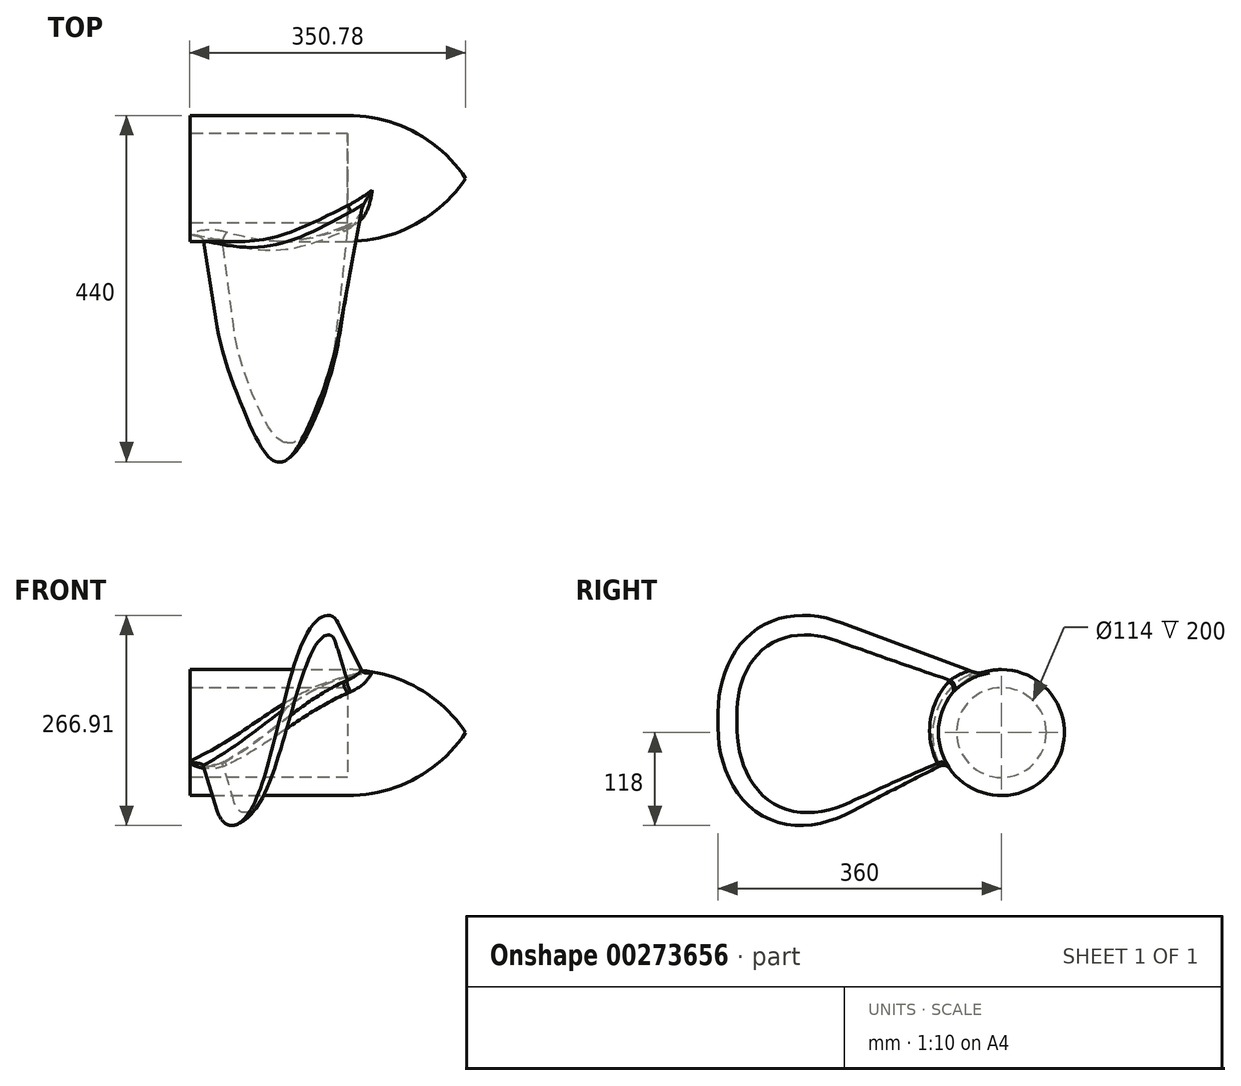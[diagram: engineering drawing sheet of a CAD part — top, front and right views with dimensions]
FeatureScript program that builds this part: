
annotation { "Feature Type Name" : "Feature", "Feature Type Description" : "" }
export const myFeature = defineFeature(function(context is Context, id is Id, definition is map)
    precondition{}
    {
        {
            var Q0;
            Q0=qCreatedBy(makeId("Front.planeOp"),FACE);
            var sketch = newSketch(context, id + "F0", { "sketchPlane" : qUnion([Q0])});
            skLineSegment(sketch, "E0", {"start": v(350, 0) * mm, "end": v(0, 0) * mm});
            skLineSegment(sketch, "E1", {"start": v(0, 0) * mm, "end": v(0, 80) * mm});
            skLineSegment(sketch, "E2", {"start": v(0, 80) * mm, "end": v(200, 80) * mm});
            skArc(sketch, "E3", {"start": v(200, 80) * mm, "mid": v(285, 58.75) * mm, "end": v(350, 0) * mm});
            skSolve(sketch);
        }
        {
            var Q0;
            Q0=makeQuery(id+"F0.imprint","IMPRINT",FACE,{"disambiguationData":[TD([[makeQuery(id+"F0.imprint","IMPRINT",EDGE,{"derivedFrom":sQuery(id+"F0.wireOp",EDGE,"E0")}),-1.0]])]});
            var Q1;
            Q1=sQuery(id+"F0.wireOp",EDGE,"E0");
            revolve(context, id + "F1", {"entities" : qUnion([Q0]), "axis" : qUnion([Q1]), "revolveType" : RevolveType.FULL});
        }
        {
            var Q0;
            Q0=qCreatedBy(makeId("Front.planeOp"),FACE);
            var sketch = newSketch(context, id + "F2", { "sketchPlane" : qUnion([Q0])});
            skLineSegment(sketch, "E4", {"start": v(3.9, 0) * mm, "end": v(225, 63.4) * mm});
            skLineSegment(sketch, "E5", {"start": v(225, 63.4) * mm, "end": v(228.3, 51.86) * mm});
            skLineSegment(sketch, "E6", {"start": v(228.3, 51.86) * mm, "end": v(7.22, -11.54) * mm});
            skLineSegment(sketch, "E7", {"start": v(7.22, -11.54) * mm, "end": v(3.9, 0) * mm});
            skSolve(sketch);
        }
        {
            var Q0;
            Q0=qCreatedBy(makeId("Front.planeOp"),FACE);
            cPlane(context, id + "F3", {"entities" : qUnion([Q0]), "cplaneType" : CPlaneType.OFFSET, "offset" : 360 * mm, "width" : 150 * mm, "height" : 150 * mm});
        }
        {
            var Q0;
            Q0=qCreatedBy(id+"F3.planeOp",FACE);
            var sketch = newSketch(context, id + "F4", { "sketchPlane" : qUnion([Q0])});
            skLineSegment(sketch, "E8", {"start": v(170.41, 195.22) * mm, "end": v(73.64, -192.9) * mm});
            skLineSegment(sketch, "E9", {"start": v(73.64, -192.9) * mm, "end": v(62, -190) * mm});
            skLineSegment(sketch, "E10", {"start": v(62, -190) * mm, "end": v(158.77, 198.12) * mm});
            skLineSegment(sketch, "E11", {"start": v(158.77, 198.12) * mm, "end": v(170.41, 195.22) * mm});
            skSolve(sketch);
        }
        {
            var Q1;
            Q1=makeQuery(id+"F4.imprint","IMPRINT",FACE,{"disambiguationData":[TD([[makeQuery(id+"F4.imprint","IMPRINT",EDGE,{"derivedFrom":sQuery(id+"F4.wireOp",EDGE,"E8")}),-1.0]])]});
            var Q2;
            Q2 = qSketchRegion(id + "F2", true);
            loft(context, id + "F5", {"operationType" : NewBodyOperationType.ADD, "sheetProfilesArray" : [{ "sheetProfileEntities" : qUnion([Q1]) }, { "sheetProfileEntities" : qUnion([Q2]) }]});
        }
        {
            var Q0;
            Q0=makeQuery(id+"F5.opLoft","MID_CAP_EDGE",EDGE,{"disambiguationData":[OSD([sQuery(id+"F4.wireOp",EDGE,"E8"),sQuery(id+"F4.wireOp",EDGE,"E10"),sQuery(id+"F4.wireOp",EDGE,"E11")])],"capPos":0.0});
            var Q1;
            Q1=makeQuery(id+"F5.opLoft","MID_CAP_EDGE",EDGE,{"disambiguationData":[OSD([sQuery(id+"F4.wireOp",EDGE,"E8"),sQuery(id+"F4.wireOp",EDGE,"E9"),sQuery(id+"F4.wireOp",EDGE,"E10")])],"capPos":0.0});
            fillet(context, id + "F6", {"entities" : qUnion([Q0, Q1]), "radius" : 135 * mm, "tangentPropagation" : true, "allowEdgeOverflow" : false});
        }
        {
            var Q0;
            Q0=makeQuery(id+"F1.opRevolve","SWEPT_FACE",FACE,{"disambiguationData":[OSD([sQuery(id+"F0.wireOp",EDGE,"E1")])]});
            var sketch = newSketch(context, id + "F7", { "sketchPlane" : qUnion([Q0])});
            skCircle(sketch, "E12", {"center": v(0, 0) * mm, "radius": 57 * mm});
            skSolve(sketch);
        }
        {
            var Q0;
            Q0=makeQuery(id+"F7.imprint","IMPRINT",FACE,{"disambiguationData":[TD([[makeQuery(id+"F7.imprint","IMPRINT",EDGE,{"derivedFrom":sQuery(id+"F7.wireOp",EDGE,"E12")}),1.0]])]});
            extrude(context, id + "F8", {"entities" : qUnion([Q0]), "operationType" : NewBodyOperationType.REMOVE, "oppositeDirection" : true, "depth" : 200 * mm});
        }
        {
            var Q0;
            {var subQ0=sQuery(id+"F4.wireOp",EDGE,"E9");var subQ1=sQuery(id+"F4.wireOp",EDGE,"E8");Q0=makeQuery(id+"F6.opFillet","BLEND_EDGE",EDGE,{"blendedFrom":[makeQuery(id+"F5.opLoft","MID_CAP_EDGE",EDGE,{"disambiguationData":[OSD([subQ1,subQ0,sQuery(id+"F4.wireOp",EDGE,"E10")])],"capPos":0.0}),makeQuery(id+"F5.opLoft","SWEPT_FACE",FACE,{"disambiguationData":[OSD([sQuery(id+"F2.wireOp",EDGE,"E5"),sQuery(id+"F2.wireOp",EDGE,"E6"),sQuery(id+"F2.wireOp",EDGE,"E7"),subQ1,subQ0,sQuery(id+"F4.wireOp",EDGE,"E11")])]})],"blendedInto":[makeQuery(id+"F5.opLoft","SWEPT_FACE",FACE,{"disambiguationData":[OSD([sQuery(id+"F2.wireOp",EDGE,"E5"),sQuery(id+"F2.wireOp",EDGE,"E6"),sQuery(id+"F2.wireOp",EDGE,"E7"),subQ1,subQ0,sQuery(id+"F4.wireOp",EDGE,"E11")])]})]});}
            fillet(context, id + "F9", {"entities" : qUnion([Q0]), "radius" : 30 * mm, "tangentPropagation" : true, "allowEdgeOverflow" : false});
        }
        {
            var Q0;
            Q0=makeQuery(id+"F5.boolean.opBoolean","INTERSECT",EDGE,{"derivedFrom":[makeQuery(id+"F1.opRevolve","SWEPT_FACE",FACE,{"disambiguationData":[OSD([sQuery(id+"F0.wireOp",EDGE,"E2")])]}),makeQuery(id+"F5.opLoft","SWEPT_FACE",FACE,{"disambiguationData":[OSD([sQuery(id+"F2.wireOp",EDGE,"E5"),sQuery(id+"F2.wireOp",EDGE,"E6"),sQuery(id+"F2.wireOp",EDGE,"E7"),sQuery(id+"F4.wireOp",EDGE,"E8"),sQuery(id+"F4.wireOp",EDGE,"E9"),sQuery(id+"F4.wireOp",EDGE,"E11")])]})]});
            var Q1;
            Q1=makeQuery(id+"F5.boolean.opBoolean","INTERSECT",EDGE,{"derivedFrom":[makeQuery(id+"F1.opRevolve","SWEPT_FACE",FACE,{"disambiguationData":[OSD([sQuery(id+"F0.wireOp",EDGE,"E2")])]}),makeQuery(id+"F5.opLoft","SWEPT_FACE",FACE,{"disambiguationData":[OSD([sQuery(id+"F2.wireOp",EDGE,"E4"),sQuery(id+"F2.wireOp",EDGE,"E5"),sQuery(id+"F2.wireOp",EDGE,"E7"),sQuery(id+"F4.wireOp",EDGE,"E9"),sQuery(id+"F4.wireOp",EDGE,"E10"),sQuery(id+"F4.wireOp",EDGE,"E11")])]})]});
            fillet(context, id + "F10", {"entities" : qUnion([Q0, Q1]), "radius" : 10 * mm, "tangentPropagation" : true, "allowEdgeOverflow" : false});
        }
    });
